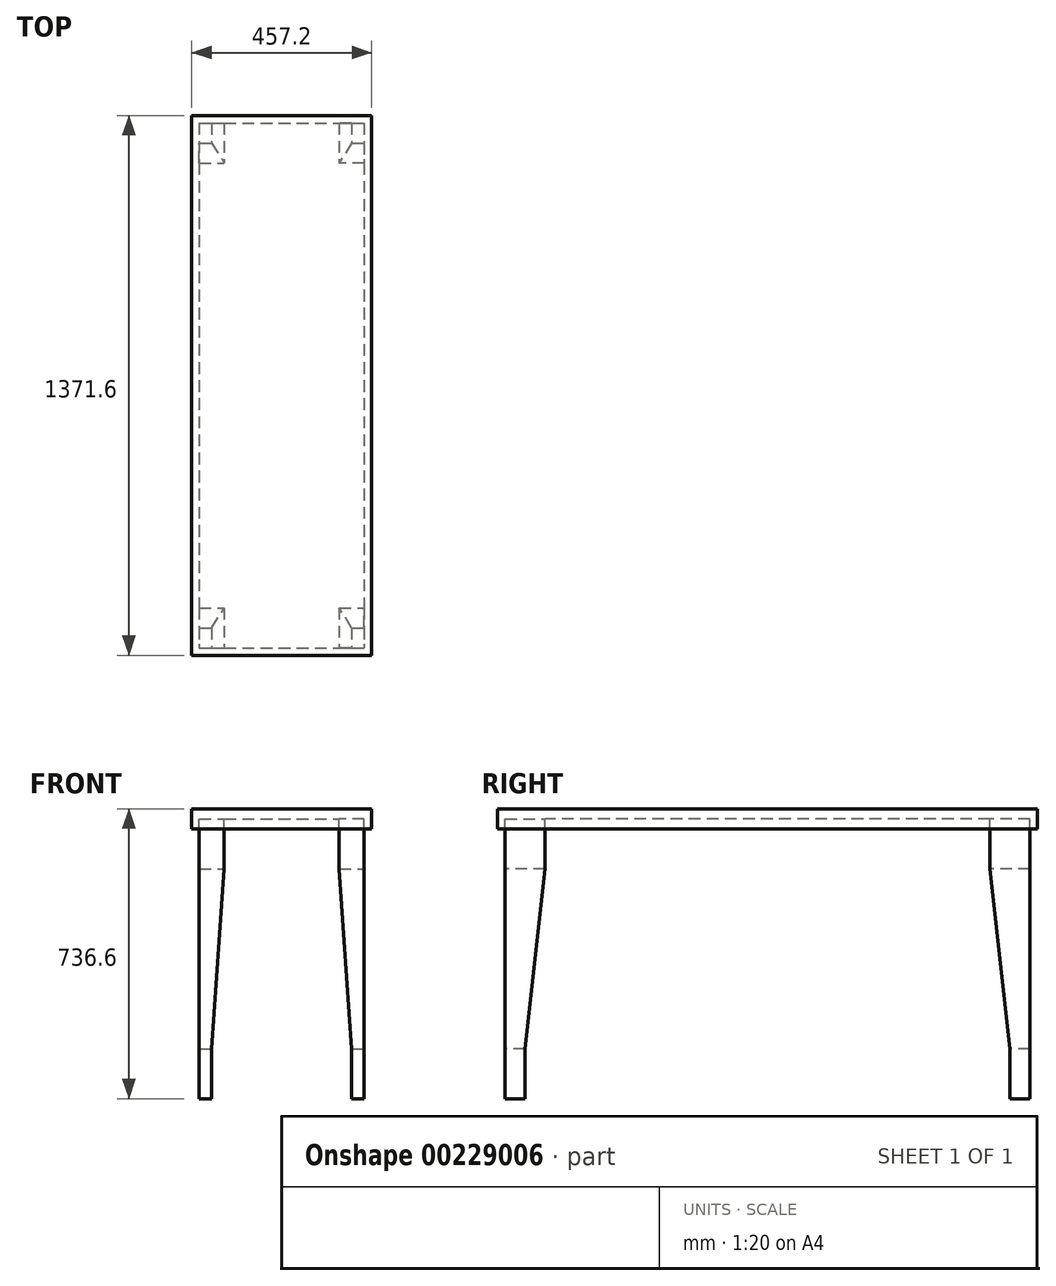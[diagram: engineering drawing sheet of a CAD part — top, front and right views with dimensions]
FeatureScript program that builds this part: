
annotation { "Feature Type Name" : "Feature", "Feature Type Description" : "" }
export const myFeature = defineFeature(function(context is Context, id is Id, definition is map)
    precondition{}
    {
        {
            var Q0;
            Q0=qCreatedBy(makeId("Top.planeOp"),FACE);
            var sketch = newSketch(context, id + "F0", { "sketchPlane" : qUnion([Q0])});
            skLineSegment(sketch, "E0.bottom", {"start": v(0, 1371.6) * mm, "end": v(457.2, 1371.6) * mm});
            skLineSegment(sketch, "E0.top", {"start": v(0, 0) * mm, "end": v(457.2, 0) * mm});
            skLineSegment(sketch, "E0.left", {"start": v(0, 1371.6) * mm, "end": v(0, 0) * mm});
            skLineSegment(sketch, "E0.right", {"start": v(457.2, 1371.6) * mm, "end": v(457.2, 0) * mm});
            skLineSegment(sketch, "E1.0", {"start": v(19.05, 1352.55) * mm, "end": v(19.05, 19.05) * mm});
            skLineSegment(sketch, "E1.1", {"start": v(19.05, 1352.55) * mm, "end": v(438.15, 1352.55) * mm});
            skLineSegment(sketch, "E1.2", {"start": v(438.15, 1352.55) * mm, "end": v(438.15, 19.05) * mm});
            skLineSegment(sketch, "E1.3", {"start": v(19.05, 19.05) * mm, "end": v(438.15, 19.05) * mm});
            skSolve(sketch);
        }
        {
            var Q0;
            Q0=makeQuery(id+"F0.imprint","IMPRINT",FACE,{"disambiguationData":[TD([[makeQuery(id+"F0.imprint","IMPRINT",EDGE,{"derivedFrom":sQuery(id+"F0.wireOp",EDGE,"E0.bottom")}),-1.0]])]});
            extrude(context, id + "F1", {"entities" : qUnion([Q0]), "depth" : 25.4 * mm});
        }
        {
            var Q0;
            Q0=makeQuery(id+"F1.opExtrude","CAP_FACE",FACE,{"disambiguationData":[OSD([sQuery(id+"F0.wireOp",EDGE,"E0.bottom"),sQuery(id+"F0.wireOp",EDGE,"E0.top"),sQuery(id+"F0.wireOp",EDGE,"E0.left"),sQuery(id+"F0.wireOp",EDGE,"E0.right"),sQuery(id+"F0.wireOp",EDGE,"E1.0"),sQuery(id+"F0.wireOp",EDGE,"E1.1"),sQuery(id+"F0.wireOp",EDGE,"E1.2"),sQuery(id+"F0.wireOp",EDGE,"E1.3")])],"isStart":false});
            var sketch = newSketch(context, id + "F2", { "sketchPlane" : qUnion([Q0])});
            skLineSegment(sketch, "E2.0", {"start": v(0, 0) * mm, "end": v(457.2, 0) * mm});
            skLineSegment(sketch, "E3.0", {"start": v(457.2, 1371.6) * mm, "end": v(457.2, 0) * mm});
            skLineSegment(sketch, "E4.0", {"start": v(0, 1371.6) * mm, "end": v(0, 0) * mm});
            skLineSegment(sketch, "E5.0", {"start": v(0, 1371.6) * mm, "end": v(457.2, 1371.6) * mm});
            skSolve(sketch);
        }
        {
            var Q0;
            Q0 = qSketchRegion(id + "F2", true);
            extrude(context, id + "F3", {"entities" : qUnion([Q0]), "operationType" : NewBodyOperationType.ADD, "depth" : 25.4 * mm});
        }
        {
            var Q0;
            Q0=makeQuery(id+"F3.opExtrude","CAP_FACE",FACE,{"disambiguationData":[OSD([sQuery(id+"F2.wireOp",EDGE,"E2.0"),sQuery(id+"F2.wireOp",EDGE,"E3.0"),sQuery(id+"F2.wireOp",EDGE,"E4.0"),sQuery(id+"F2.wireOp",EDGE,"E5.0")])],"isStart":true});
            var sketch = newSketch(context, id + "F4", { "sketchPlane" : qUnion([Q0])});
            skLineSegment(sketch, "E6.bottom", {"start": v(19.05, -19.05) * mm, "end": v(82.55, -19.05) * mm});
            skLineSegment(sketch, "E6.top", {"start": v(19.05, -120.65) * mm, "end": v(82.55, -120.65) * mm});
            skLineSegment(sketch, "E6.left", {"start": v(19.05, -19.05) * mm, "end": v(19.05, -120.65) * mm});
            skLineSegment(sketch, "E6.right", {"start": v(82.55, -19.05) * mm, "end": v(82.55, -120.65) * mm});
            skLineSegment(sketch, "E7.bottom", {"start": v(438.15, -19.05) * mm, "end": v(374.65, -19.05) * mm});
            skLineSegment(sketch, "E7.top", {"start": v(438.15, -120.65) * mm, "end": v(374.65, -120.65) * mm});
            skLineSegment(sketch, "E7.left", {"start": v(438.15, -19.05) * mm, "end": v(438.15, -120.65) * mm});
            skLineSegment(sketch, "E7.right", {"start": v(374.65, -19.05) * mm, "end": v(374.65, -120.65) * mm});
            skLineSegment(sketch, "E8.bottom", {"start": v(19.05, -1352.55) * mm, "end": v(82.55, -1352.55) * mm});
            skLineSegment(sketch, "E8.top", {"start": v(19.05, -1250.95) * mm, "end": v(82.55, -1250.95) * mm});
            skLineSegment(sketch, "E8.left", {"start": v(19.05, -1352.55) * mm, "end": v(19.05, -1250.95) * mm});
            skLineSegment(sketch, "E8.right", {"start": v(82.55, -1352.55) * mm, "end": v(82.55, -1250.95) * mm});
            skLineSegment(sketch, "E9.bottom", {"start": v(438.15, -1352.55) * mm, "end": v(374.65, -1352.55) * mm});
            skLineSegment(sketch, "E9.top", {"start": v(438.15, -1250.95) * mm, "end": v(374.65, -1250.95) * mm});
            skLineSegment(sketch, "E9.left", {"start": v(438.15, -1352.55) * mm, "end": v(438.15, -1250.95) * mm});
            skLineSegment(sketch, "E9.right", {"start": v(374.65, -1352.55) * mm, "end": v(374.65, -1250.95) * mm});
            skSolve(sketch);
        }
        {
            var Q0;
            Q0 = qSketchRegion(id + "F4", true);
            extrude(context, id + "F5", {"entities" : qUnion([Q0]), "operationType" : NewBodyOperationType.ADD, "depth" : 711.2 * mm});
        }
        {
            var Q0;
            Q0=makeQuery(id+"F5.opExtrude","SWEPT_FACE",FACE,{"disambiguationData":[OSD([sQuery(id+"F4.wireOp",EDGE,"E6.bottom")])]});
            var sketch = newSketch(context, id + "F6", { "sketchPlane" : qUnion([Q0])});
            skLineSegment(sketch, "E10", {"start": v(50.8, -685.8) * mm, "end": v(50.8, -558.8) * mm});
            skLineSegment(sketch, "E11", {"start": v(50.8, -558.8) * mm, "end": v(82.55, -101.6) * mm});
            skLineSegment(sketch, "E12", {"start": v(228.6, 0) * mm, "end": v(228.6, -99.07) * mm});
            skLineSegment(sketch, "E13.MirrorCS", {"start": v(406.4, -558.8) * mm, "end": v(374.65, -101.6) * mm});
            skLineSegment(sketch, "E14.MirrorCS", {"start": v(406.4, -685.8) * mm, "end": v(406.4, -558.8) * mm});
            skLineSegment(sketch, "E15", {"start": v(82.55, -101.6) * mm, "end": v(374.65, -101.6) * mm});
            skLineSegment(sketch, "E16", {"start": v(406.4, -685.8) * mm, "end": v(50.8, -685.8) * mm});
            skSolve(sketch);
        }
        {
            var Q0;
            Q0 = qSketchRegion(id + "F6", true);
            extrude(context, id + "F7", {"entities" : qUnion([Q0]), "operationType" : NewBodyOperationType.REMOVE, "endBound" : BoundingType.THROUGH_ALL, "oppositeDirection" : true, "depth" : 25.4 * mm});
        }
        {
            var Q0;
            Q0=makeQuery(id+"F5.opExtrude","SWEPT_FACE",FACE,{"disambiguationData":[OSD([sQuery(id+"F4.wireOp",EDGE,"E7.left")])]});
            var sketch = newSketch(context, id + "F8", { "sketchPlane" : qUnion([Q0])});
            skLineSegment(sketch, "E17", {"start": v(69.85, -685.8) * mm, "end": v(69.85, -558.8) * mm});
            skLineSegment(sketch, "E18", {"start": v(69.85, -558.8) * mm, "end": v(120.65, -101.6) * mm});
            skLineSegment(sketch, "E19", {"start": v(120.65, -101.6) * mm, "end": v(120.65, 0) * mm});
            skLineSegment(sketch, "E20", {"start": v(685.8, 0) * mm, "end": v(685.8, -72.83) * mm});
            skLineSegment(sketch, "E21.MirrorCS", {"start": v(1301.75, -558.8) * mm, "end": v(1250.95, -101.6) * mm});
            skLineSegment(sketch, "E22.MirrorCS", {"start": v(1301.75, -685.8) * mm, "end": v(1301.75, -558.8) * mm});
            skLineSegment(sketch, "E23", {"start": v(120.65, -101.6) * mm, "end": v(1250.95, -101.6) * mm});
            skLineSegment(sketch, "E24", {"start": v(1301.75, -685.8) * mm, "end": v(69.85, -685.8) * mm});
            skSolve(sketch);
        }
        {
            var Q0;
            Q0 = qSketchRegion(id + "F8", true);
            extrude(context, id + "F9", {"entities" : qUnion([Q0]), "operationType" : NewBodyOperationType.REMOVE, "endBound" : BoundingType.THROUGH_ALL, "oppositeDirection" : true, "depth" : 25.4 * mm});
        }
    });
